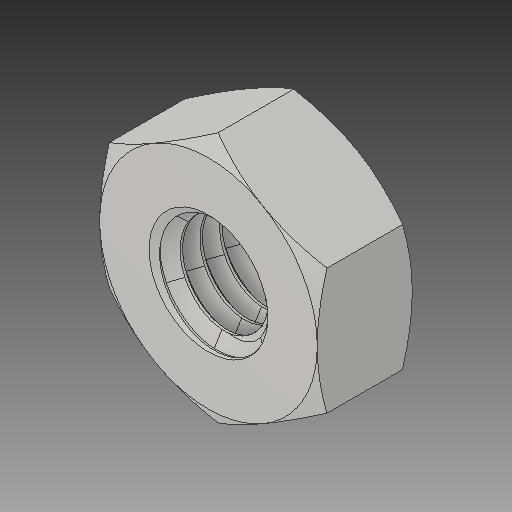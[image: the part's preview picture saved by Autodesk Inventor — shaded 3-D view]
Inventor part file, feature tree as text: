
AUTODESK INVENTOR PART (.ipt)
format: ipt  version: 2019 (Build 230136000, 136)  size: 444,416 bytes
history: imported  units: mm
features: imported_body x1
ambient origin geometry x8: Origin, YZ Plane, XZ Plane, XY Plane, X Axis, Y Axis, Z Axis, Center Point
bodies: Solide1 (imported_parasolid), Body1 (imported_parasolid)
feature tree (1):
  imported_body  NMx_Import_Brep_tag  [imported B-rep: ~3 faces, bbox_mm=None]
